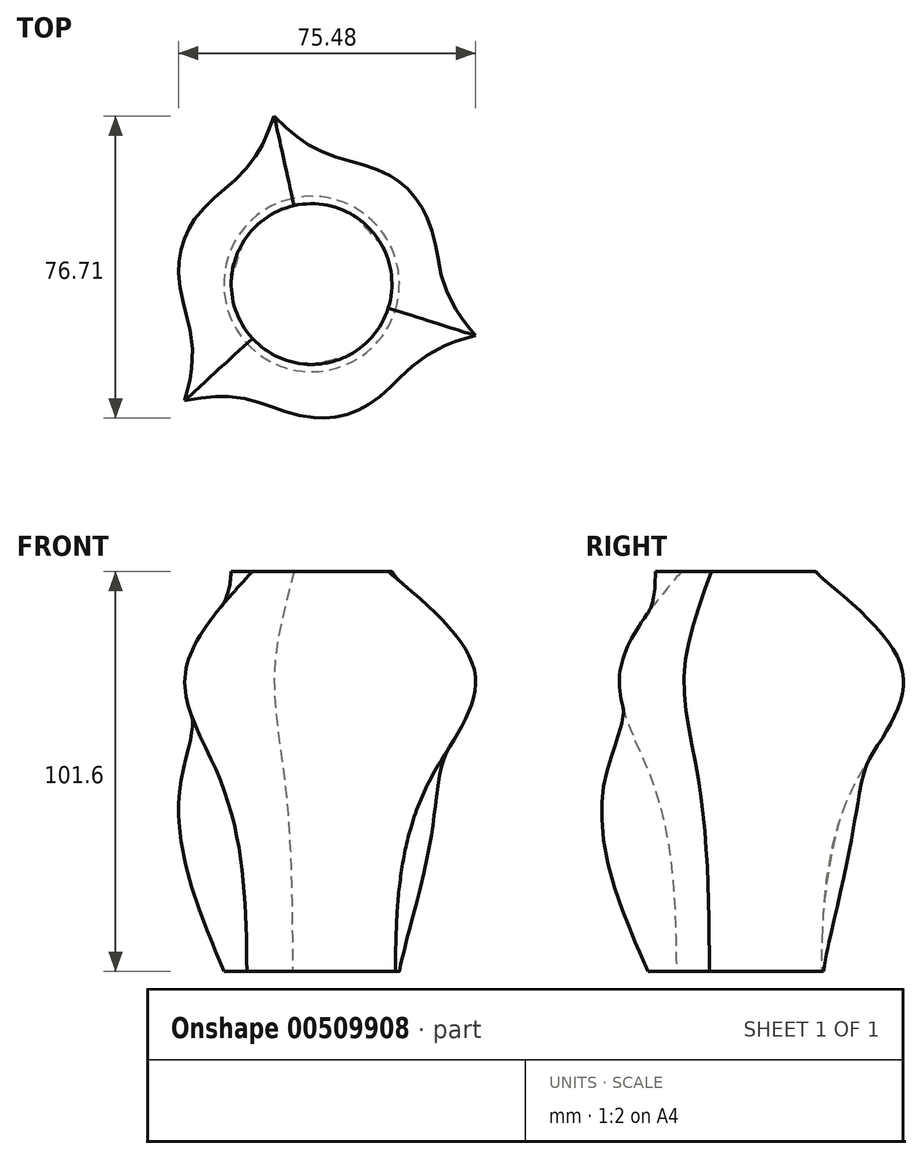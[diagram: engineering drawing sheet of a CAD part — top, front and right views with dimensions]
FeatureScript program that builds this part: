
annotation { "Feature Type Name" : "Feature", "Feature Type Description" : "" }
export const myFeature = defineFeature(function(context is Context, id is Id, definition is map)
    precondition{}
    {
        {
            var Q0;
            Q0=qCreatedBy(makeId("Top.planeOp"),FACE);
            cPlane(context, id + "F0", {"entities" : qUnion([Q0]), "cplaneType" : CPlaneType.OFFSET, "offset" : 25.4 * mm, "width" : 152.4 * mm, "height" : 152.4 * mm});
        }
        {
            var Q0;
            Q0=qCreatedBy(id+"F0.planeOp",FACE);
            cPlane(context, id + "F1", {"entities" : qUnion([Q0]), "cplaneType" : CPlaneType.OFFSET, "offset" : 25.4 * mm, "width" : 152.4 * mm, "height" : 152.4 * mm});
        }
        {
            var Q0;
            Q0=qCreatedBy(makeId("Top.planeOp"),FACE);
            cPlane(context, id + "F2", {"entities" : qUnion([Q0]), "cplaneType" : CPlaneType.OFFSET, "offset" : 25.4 * mm, "oppositeDirection" : true, "width" : 152.4 * mm, "height" : 152.4 * mm});
        }
        {
            var Q0;
            Q0=qCreatedBy(id+"F2.planeOp",FACE);
            cPlane(context, id + "F3", {"entities" : qUnion([Q0]), "cplaneType" : CPlaneType.OFFSET, "offset" : 25.4 * mm, "oppositeDirection" : true, "width" : 152.4 * mm, "height" : 152.4 * mm});
        }
        {
            var Q0;
            Q0=qCreatedBy(id+"F3.planeOp",FACE);
            var sketch = newSketch(context, id + "F4", { "sketchPlane" : qUnion([Q0])});
            skCircle(sketch, "E0", {"center": v(0, 0) * mm, "radius": 22.3 * mm});
            skSolve(sketch);
        }
        {
            var Q0;
            Q0=qCreatedBy(makeId("Top.planeOp"),FACE);
            var sketch = newSketch(context, id + "F5", { "sketchPlane" : qUnion([Q0])});
            skCircle(sketch, "E1", {"center": v(0, 0) * mm, "radius": 32.73 * mm});
            skSolve(sketch);
        }
        {
            var Q0;
            Q0=qCreatedBy(id+"F0.planeOp",FACE);
            var sketch = newSketch(context, id + "F6", { "sketchPlane" : qUnion([Q0])});
            skCircle(sketch, "E2.cCircle", {"center": v(0, 0) * mm, "radius": 21.72 * mm, "construction": true});
            skLineSegment(sketch, "E2.0", {"start": v(41.44, -13.02) * mm, "end": v(-32, -29.38) * mm});
            skLineSegment(sketch, "E2.1", {"start": v(-32, -29.38) * mm, "end": v(-9.44, 42.4) * mm});
            skLineSegment(sketch, "E2.2", {"start": v(-9.44, 42.4) * mm, "end": v(41.44, -13.02) * mm});
            skPoint(sketch, "E2.0.midPoint", {"position": v(4.72, -21.2) * mm});
            skSolve(sketch);
        }
        {
            var Q0;
            Q0=qCreatedBy(id+"F1.planeOp",FACE);
            var sketch = newSketch(context, id + "F7", { "sketchPlane" : qUnion([Q0])});
            skCircle(sketch, "E3", {"center": v(0, 0) * mm, "radius": 20.4 * mm});
            skSolve(sketch);
        }
        {
            var Q0;
            Q0=makeQuery(id+"F7.imprint","IMPRINT",FACE,{"disambiguationData":[TD([[makeQuery(id+"F7.imprint","IMPRINT",EDGE,{"derivedFrom":sQuery(id+"F7.wireOp",EDGE,"E3")}),1.0]])]});
            var Q1;
            Q1=makeQuery(id+"F6.imprint","IMPRINT",FACE,{"disambiguationData":[TD([[makeQuery(id+"F6.imprint","IMPRINT",EDGE,{"derivedFrom":sQuery(id+"F6.wireOp",EDGE,"E2.0")}),-1.0]])]});
            var Q2;
            Q2=makeQuery(id+"F5.imprint","IMPRINT",FACE,{"disambiguationData":[TD([[makeQuery(id+"F5.imprint","IMPRINT",EDGE,{"derivedFrom":sQuery(id+"F5.wireOp",EDGE,"E1")}),1.0]])]});
            var Q3;
            Q3=makeQuery(id+"F4.imprint","IMPRINT",FACE,{"disambiguationData":[TD([[makeQuery(id+"F4.imprint","IMPRINT",EDGE,{"derivedFrom":sQuery(id+"F4.wireOp",EDGE,"E0")}),1.0]])]});
            loft(context, id + "F8", {"sheetProfilesArray" : [{ "sheetProfileEntities" : qUnion([Q0]) }, { "sheetProfileEntities" : qUnion([Q1]) }, { "sheetProfileEntities" : qUnion([Q2]) }, { "sheetProfileEntities" : qUnion([Q3]) }]});
        }
    });
